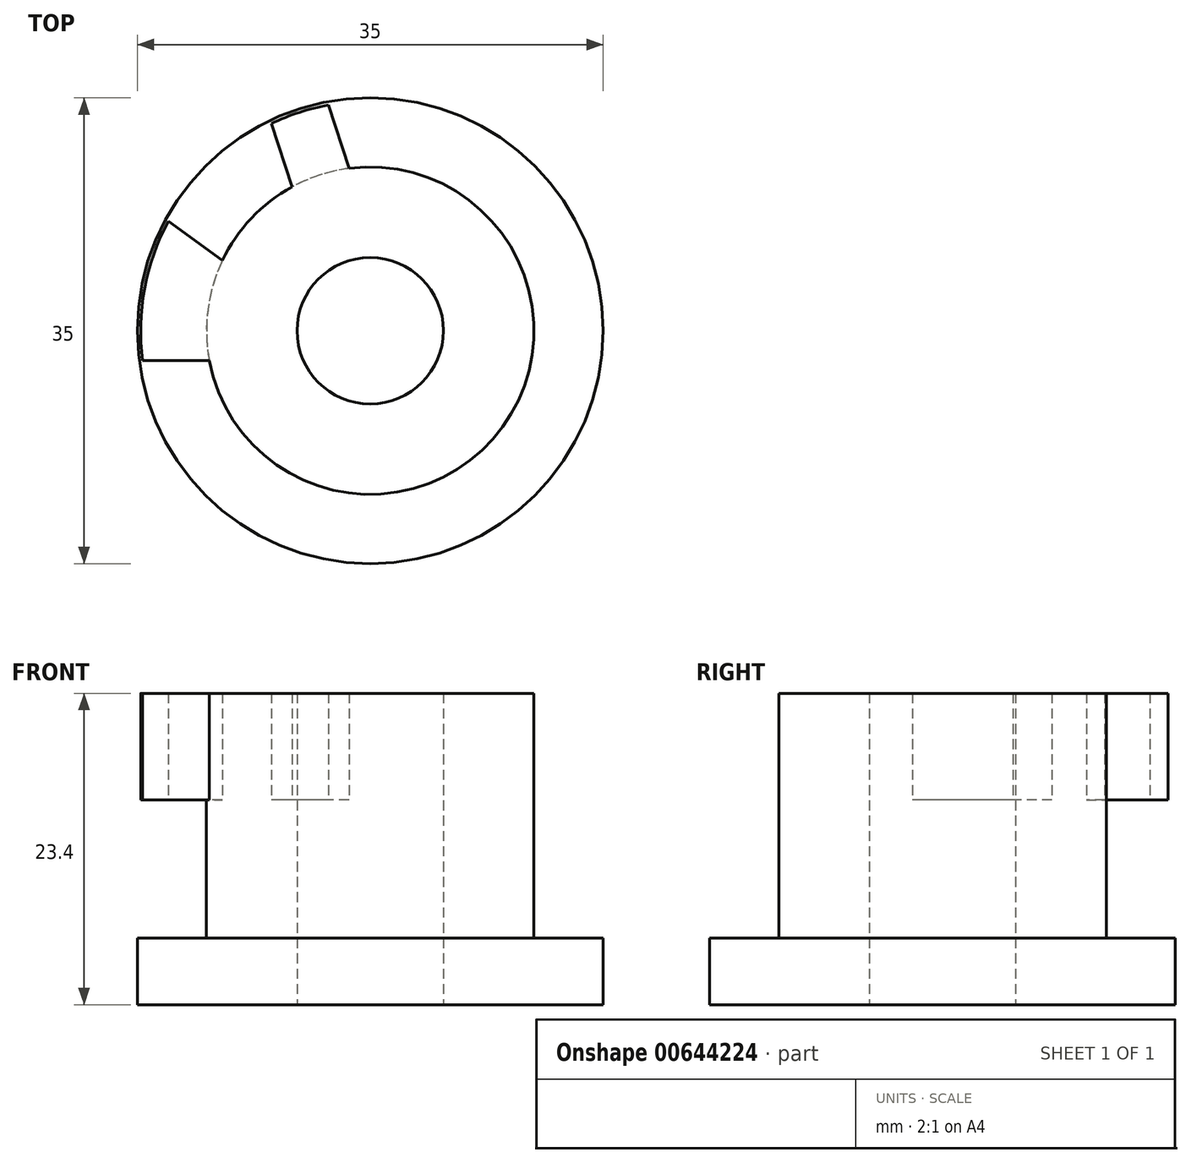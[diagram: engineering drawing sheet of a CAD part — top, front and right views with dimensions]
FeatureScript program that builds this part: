
annotation { "Feature Type Name" : "Feature", "Feature Type Description" : "" }
export const myFeature = defineFeature(function(context is Context, id is Id, definition is map)
    precondition{}
    {
        {
            var Q0;
            Q0=qCreatedBy(makeId("Top.planeOp"),FACE);
            var sketch = newSketch(context, id + "F0", { "sketchPlane" : qUnion([Q0])});
            skCircle(sketch, "E0", {"center": v(0, 0) * mm, "radius": 17.5 * mm});
            skCircle(sketch, "E1", {"center": v(0, 0) * mm, "radius": 5.5 * mm});
            skSolve(sketch);
        }
        {
            var Q0;
            Q0=makeQuery(id+"F0.imprint","IMPRINT",FACE,{"disambiguationData":[TD([[makeQuery(id+"F0.imprint","IMPRINT",EDGE,{"derivedFrom":sQuery(id+"F0.wireOp",EDGE,"E0")}),1.0]])]});
            extrude(context, id + "F1", {"entities" : qUnion([Q0]), "depth" : 5 * mm, "offsetDistance" : 25 * mm});
        }
        {
            var Q0;
            Q0=makeQuery(id+"F1.opExtrude","CAP_FACE",FACE,{"disambiguationData":[OSD([sQuery(id+"F0.wireOp",EDGE,"E0")])],"isStart":false});
            var sketch = newSketch(context, id + "F2", { "sketchPlane" : qUnion([Q0])});
            skCircle(sketch, "E2", {"center": v(0, 0) * mm, "radius": 12.3 * mm});
            skSolve(sketch);
        }
        {
            var Q0;
            Q0=makeQuery(id+"F2.imprint","IMPRINT",FACE,{"disambiguationData":[TD([[makeQuery(id+"F2.imprint","IMPRINT",EDGE,{"derivedFrom":sQuery(id+"F2.wireOp",EDGE,"E2")}),1.0]])]});
            var Q1;
            Q1=sQuery(id+"F2.wireOp",EDGE,"E2");
            extrude(context, id + "F3", {"entities" : qUnion([Q0]), "surfaceEntities" : qUnion([Q1]), "depth" : 10.4 * mm, "offsetDistance" : 25 * mm});
        }
        {
            var Q0;
            Q0=makeQuery(id+"F3.opExtrude","CAP_FACE",FACE,{"disambiguationData":[OSD([sQuery(id+"F2.wireOp",EDGE,"E2")])],"isStart":false});
            var sketch = newSketch(context, id + "F4", { "sketchPlane" : qUnion([Q0])});
            skPoint(sketch, "E3.middle", {"position": v(0, 0) * mm});
            skLineSegment(sketch, "E4.bottom", {"start": v(24.05, -2.25) * mm, "end": v(-24.05, -2.25) * mm});
            skLineSegment(sketch, "E4.top", {"start": v(24.05, 2.25) * mm, "end": v(-24.05, 2.25) * mm});
            skLineSegment(sketch, "E4.left", {"start": v(24.05, -2.25) * mm, "end": v(24.05, 2.25) * mm});
            skLineSegment(sketch, "E4.right", {"start": v(-24.05, -2.25) * mm, "end": v(-24.05, 2.25) * mm});
            skCircle(sketch, "E5", {"center": v(0, 0) * mm, "radius": 17.25 * mm});
            skLineSegment(sketch, "E6.1.0", {"start": v(5.3, 23.57) * mm, "end": v(-9.57, -22.18) * mm});
            skLineSegment(sketch, "E6.1.1", {"start": v(-5.3, -23.57) * mm, "end": v(-9.57, -22.18) * mm});
            skLineSegment(sketch, "E6.1.2", {"start": v(9.57, 22.18) * mm, "end": v(-5.3, -23.57) * mm});
            skLineSegment(sketch, "E6.1.3", {"start": v(9.57, 22.18) * mm, "end": v(5.3, 23.57) * mm});
            skLineSegment(sketch, "E6.2.0", {"start": v(-20.78, 12.32) * mm, "end": v(18.14, -15.96) * mm});
            skLineSegment(sketch, "E6.2.1", {"start": v(20.78, -12.32) * mm, "end": v(18.14, -15.96) * mm});
            skLineSegment(sketch, "E6.2.2", {"start": v(-18.14, 15.96) * mm, "end": v(20.78, -12.32) * mm});
            skLineSegment(sketch, "E6.2.3", {"start": v(-18.14, 15.96) * mm, "end": v(-20.78, 12.32) * mm});
            skLineSegment(sketch, "E6.3.0", {"start": v(-18.14, -15.96) * mm, "end": v(20.78, 12.32) * mm});
            skLineSegment(sketch, "E6.3.1", {"start": v(18.14, 15.96) * mm, "end": v(20.78, 12.32) * mm});
            skLineSegment(sketch, "E6.3.2", {"start": v(-20.78, -12.32) * mm, "end": v(18.14, 15.96) * mm});
            skLineSegment(sketch, "E6.3.3", {"start": v(-20.78, -12.32) * mm, "end": v(-18.14, -15.96) * mm});
            skLineSegment(sketch, "E6.4.0", {"start": v(9.57, -22.18) * mm, "end": v(-5.3, 23.57) * mm});
            skLineSegment(sketch, "E6.4.1", {"start": v(-9.57, 22.18) * mm, "end": v(-5.3, 23.57) * mm});
            skLineSegment(sketch, "E6.4.2", {"start": v(5.3, -23.57) * mm, "end": v(-9.57, 22.18) * mm});
            skLineSegment(sketch, "E6.4.3", {"start": v(5.3, -23.57) * mm, "end": v(9.57, -22.18) * mm});
            skSolve(sketch);
        }
        {
            var Q0;
            {var subQ0=sQuery(id+"F4.wireOp",EDGE,"E6.4.0");var subQ1=sQuery(id+"F4.wireOp",EDGE,"E5");var subQ2=makeQuery(id+"F4.imprint","INTERSECT",VERTEX,{"disambiguationData":[OD(0.0)],"derivedFrom":[subQ1,subQ0]});Q0=makeQuery(id+"F4.imprint","IMPRINT",FACE,{"disambiguationData":[TD([[makeQuery(id+"F4.imprint","IMPRINT",EDGE,{"disambiguationData":[TD([[subQ2,-1.0]])],"derivedFrom":subQ1}),1.0]])]});}
            var Q1;
            {var subQ0=sQuery(id+"F4.wireOp",EDGE,"E5");var subQ1=sQuery(id+"F4.wireOp",EDGE,"E4.bottom");var subQ2=makeQuery(id+"F4.imprint","INTERSECT",VERTEX,{"disambiguationData":[OD(1.0)],"derivedFrom":[subQ1,subQ0]});Q1=makeQuery(id+"F4.imprint","IMPRINT",FACE,{"disambiguationData":[TD([[makeQuery(id+"F4.imprint","IMPRINT",EDGE,{"disambiguationData":[TD([[subQ2,1.0]])],"derivedFrom":subQ1}),-1.0]])]});}
            var Q2;
            {var subQ0=sQuery(id+"F4.wireOp",EDGE,"E6.2.0");var subQ1=sQuery(id+"F4.wireOp",EDGE,"E5");var subQ2=makeQuery(id+"F4.imprint","INTERSECT",VERTEX,{"disambiguationData":[OD(1.0)],"derivedFrom":[subQ1,subQ0]});Q2=makeQuery(id+"F4.imprint","IMPRINT",FACE,{"disambiguationData":[TD([[makeQuery(id+"F4.imprint","IMPRINT",EDGE,{"disambiguationData":[TD([[subQ2,-1.0]])],"derivedFrom":subQ1}),1.0]])]});}
            var Q3;
            {var subQ0=sQuery(id+"F4.wireOp",EDGE,"E6.2.2");var subQ1=sQuery(id+"F4.wireOp",EDGE,"E4.bottom");var subQ2=makeQuery(id+"F4.imprint","INTERSECT",VERTEX,{"derivedFrom":[subQ1,subQ0]});Q3=makeQuery(id+"F4.imprint","IMPRINT",FACE,{"disambiguationData":[TD([[makeQuery(id+"F4.imprint","IMPRINT",EDGE,{"disambiguationData":[TD([[subQ2,-1.0]])],"derivedFrom":subQ1}),1.0]])]});}
            var Q4;
            {var subQ0=sQuery(id+"F4.wireOp",EDGE,"E6.2.2");var subQ1=sQuery(id+"F4.wireOp",EDGE,"E4.bottom");var subQ2=makeQuery(id+"F4.imprint","INTERSECT",VERTEX,{"derivedFrom":[subQ1,subQ0]});Q4=makeQuery(id+"F4.imprint","IMPRINT",FACE,{"disambiguationData":[TD([[makeQuery(id+"F4.imprint","IMPRINT",EDGE,{"disambiguationData":[TD([[subQ2,1.0]])],"derivedFrom":subQ1}),1.0]])]});}
            var Q5;
            {var subQ0=sQuery(id+"F4.wireOp",EDGE,"E6.2.2");var subQ1=sQuery(id+"F4.wireOp",EDGE,"E4.bottom");var subQ2=makeQuery(id+"F4.imprint","INTERSECT",VERTEX,{"derivedFrom":[subQ1,subQ0]});Q5=makeQuery(id+"F4.imprint","IMPRINT",FACE,{"disambiguationData":[TD([[makeQuery(id+"F4.imprint","IMPRINT",EDGE,{"disambiguationData":[TD([[subQ2,1.0]])],"derivedFrom":subQ1}),-1.0]])]});}
            var Q6;
            {var subQ0=sQuery(id+"F4.wireOp",EDGE,"E6.3.0");var subQ1=sQuery(id+"F4.wireOp",EDGE,"E4.top");var subQ2=makeQuery(id+"F4.imprint","INTERSECT",VERTEX,{"derivedFrom":[subQ1,subQ0]});Q6=makeQuery(id+"F4.imprint","IMPRINT",FACE,{"disambiguationData":[TD([[makeQuery(id+"F4.imprint","IMPRINT",EDGE,{"disambiguationData":[TD([[subQ2,1.0]])],"derivedFrom":subQ1}),-1.0]])]});}
            var Q7;
            {var subQ7=sQuery(id+"F4.wireOp",EDGE,"E6.3.0");var subQ8=sQuery(id+"F4.wireOp",EDGE,"E4.top");var subQ9=makeQuery(id+"F4.imprint","INTERSECT",VERTEX,{"derivedFrom":[subQ8,subQ7]});Q7=makeQuery(id+"F4.imprint","IMPRINT",FACE,{"disambiguationData":[TD([[makeQuery(id+"F4.imprint","IMPRINT",EDGE,{"disambiguationData":[TD([[subQ9,-1.0]])],"derivedFrom":subQ8}),-1.0]])]});}
            var Q8;
            {var subQ0=sQuery(id+"F4.wireOp",EDGE,"E6.3.2");var subQ1=sQuery(id+"F4.wireOp",EDGE,"E6.1.2");var subQ2=makeQuery(id+"F4.imprint","INTERSECT",VERTEX,{"derivedFrom":[subQ1,subQ0]});Q8=makeQuery(id+"F4.imprint","IMPRINT",FACE,{"disambiguationData":[TD([[makeQuery(id+"F4.imprint","IMPRINT",EDGE,{"disambiguationData":[TD([[subQ2,1.0]])],"derivedFrom":subQ1}),1.0]])]});}
            var Q9;
            {var subQ7=sQuery(id+"F4.wireOp",EDGE,"E6.4.0");var subQ8=sQuery(id+"F4.wireOp",EDGE,"E6.1.0");var subQ9=makeQuery(id+"F4.imprint","INTERSECT",VERTEX,{"derivedFrom":[subQ8,subQ7]});Q9=makeQuery(id+"F4.imprint","IMPRINT",FACE,{"disambiguationData":[TD([[makeQuery(id+"F4.imprint","IMPRINT",EDGE,{"disambiguationData":[TD([[subQ9,1.0]])],"derivedFrom":subQ8}),1.0]])]});}
            var Q10;
            {var subQ0=sQuery(id+"F4.wireOp",EDGE,"E6.4.0");var subQ1=sQuery(id+"F4.wireOp",EDGE,"E6.1.0");var subQ2=makeQuery(id+"F4.imprint","INTERSECT",VERTEX,{"derivedFrom":[subQ1,subQ0]});Q10=makeQuery(id+"F4.imprint","IMPRINT",FACE,{"disambiguationData":[TD([[makeQuery(id+"F4.imprint","IMPRINT",EDGE,{"disambiguationData":[TD([[subQ2,1.0]])],"derivedFrom":subQ1}),-1.0]])]});}
            var Q11;
            {var subQ5=sQuery(id+"F4.wireOp",EDGE,"E6.4.0");var subQ6=sQuery(id+"F4.wireOp",EDGE,"E6.1.0");var subQ7=makeQuery(id+"F4.imprint","INTERSECT",VERTEX,{"derivedFrom":[subQ6,subQ5]});Q11=makeQuery(id+"F4.imprint","IMPRINT",FACE,{"disambiguationData":[TD([[makeQuery(id+"F4.imprint","IMPRINT",EDGE,{"disambiguationData":[TD([[subQ7,-1.0]])],"derivedFrom":subQ6}),-1.0]])]});}
            var Q12;
            {var subQ0=sQuery(id+"F4.wireOp",EDGE,"E6.4.2");var subQ1=sQuery(id+"F4.wireOp",EDGE,"E6.2.2");var subQ2=makeQuery(id+"F4.imprint","INTERSECT",VERTEX,{"derivedFrom":[subQ1,subQ0]});Q12=makeQuery(id+"F4.imprint","IMPRINT",FACE,{"disambiguationData":[TD([[makeQuery(id+"F4.imprint","IMPRINT",EDGE,{"disambiguationData":[TD([[subQ2,1.0]])],"derivedFrom":subQ1}),1.0]])]});}
            var Q13;
            {var subQ7=sQuery(id+"F4.wireOp",EDGE,"E6.2.0");var subQ8=sQuery(id+"F4.wireOp",EDGE,"E4.top");var subQ9=makeQuery(id+"F4.imprint","INTERSECT",VERTEX,{"derivedFrom":[subQ8,subQ7]});Q13=makeQuery(id+"F4.imprint","IMPRINT",FACE,{"disambiguationData":[TD([[makeQuery(id+"F4.imprint","IMPRINT",EDGE,{"disambiguationData":[TD([[subQ9,1.0]])],"derivedFrom":subQ8}),-1.0]])]});}
            var Q14;
            {var subQ0=sQuery(id+"F4.wireOp",EDGE,"E6.2.0");var subQ1=sQuery(id+"F4.wireOp",EDGE,"E4.top");var subQ2=makeQuery(id+"F4.imprint","INTERSECT",VERTEX,{"derivedFrom":[subQ1,subQ0]});Q14=makeQuery(id+"F4.imprint","IMPRINT",FACE,{"disambiguationData":[TD([[makeQuery(id+"F4.imprint","IMPRINT",EDGE,{"disambiguationData":[TD([[subQ2,-1.0]])],"derivedFrom":subQ1}),-1.0]])]});}
            var Q15;
            {var subQ0=sQuery(id+"F4.wireOp",EDGE,"E6.3.2");var subQ1=sQuery(id+"F4.wireOp",EDGE,"E4.bottom");var subQ2=makeQuery(id+"F4.imprint","INTERSECT",VERTEX,{"derivedFrom":[subQ1,subQ0]});Q15=makeQuery(id+"F4.imprint","IMPRINT",FACE,{"disambiguationData":[TD([[makeQuery(id+"F4.imprint","IMPRINT",EDGE,{"disambiguationData":[TD([[subQ2,-1.0]])],"derivedFrom":subQ1}),-1.0]])]});}
            var Q16;
            {var subQ0=sQuery(id+"F4.wireOp",EDGE,"E6.3.2");var subQ1=sQuery(id+"F4.wireOp",EDGE,"E4.bottom");var subQ2=makeQuery(id+"F4.imprint","INTERSECT",VERTEX,{"derivedFrom":[subQ1,subQ0]});Q16=makeQuery(id+"F4.imprint","IMPRINT",FACE,{"disambiguationData":[TD([[makeQuery(id+"F4.imprint","IMPRINT",EDGE,{"disambiguationData":[TD([[subQ2,-1.0]])],"derivedFrom":subQ1}),1.0]])]});}
            var Q17;
            {var subQ0=sQuery(id+"F4.wireOp",EDGE,"E6.3.2");var subQ1=sQuery(id+"F4.wireOp",EDGE,"E4.bottom");var subQ2=makeQuery(id+"F4.imprint","INTERSECT",VERTEX,{"derivedFrom":[subQ1,subQ0]});Q17=makeQuery(id+"F4.imprint","IMPRINT",FACE,{"disambiguationData":[TD([[makeQuery(id+"F4.imprint","IMPRINT",EDGE,{"disambiguationData":[TD([[subQ2,1.0]])],"derivedFrom":subQ1}),1.0]])]});}
            var Q18;
            {var subQ0=sQuery(id+"F4.wireOp",EDGE,"E6.3.0");var subQ1=sQuery(id+"F4.wireOp",EDGE,"E6.1.0");var subQ2=makeQuery(id+"F4.imprint","INTERSECT",VERTEX,{"derivedFrom":[subQ1,subQ0]});Q18=makeQuery(id+"F4.imprint","IMPRINT",FACE,{"disambiguationData":[TD([[makeQuery(id+"F4.imprint","IMPRINT",EDGE,{"disambiguationData":[TD([[subQ2,-1.0]])],"derivedFrom":subQ1}),-1.0]])]});}
            var Q19;
            {var subQ7=sQuery(id+"F4.wireOp",EDGE,"E6.3.0");var subQ8=sQuery(id+"F4.wireOp",EDGE,"E6.1.0");var subQ9=makeQuery(id+"F4.imprint","INTERSECT",VERTEX,{"derivedFrom":[subQ8,subQ7]});Q19=makeQuery(id+"F4.imprint","IMPRINT",FACE,{"disambiguationData":[TD([[makeQuery(id+"F4.imprint","IMPRINT",EDGE,{"disambiguationData":[TD([[subQ9,-1.0]])],"derivedFrom":subQ8}),1.0]])]});}
            var Q20;
            {var subQ0=sQuery(id+"F4.wireOp",EDGE,"E6.4.2");var subQ1=sQuery(id+"F4.wireOp",EDGE,"E6.1.2");var subQ2=makeQuery(id+"F4.imprint","INTERSECT",VERTEX,{"derivedFrom":[subQ1,subQ0]});Q20=makeQuery(id+"F4.imprint","IMPRINT",FACE,{"disambiguationData":[TD([[makeQuery(id+"F4.imprint","IMPRINT",EDGE,{"disambiguationData":[TD([[subQ2,-1.0]])],"derivedFrom":subQ1}),1.0]])]});}
            var Q21;
            {var subQ0=sQuery(id+"F4.wireOp",EDGE,"E6.4.2");var subQ1=sQuery(id+"F4.wireOp",EDGE,"E6.1.2");var subQ2=makeQuery(id+"F4.imprint","INTERSECT",VERTEX,{"derivedFrom":[subQ1,subQ0]});Q21=makeQuery(id+"F4.imprint","IMPRINT",FACE,{"disambiguationData":[TD([[makeQuery(id+"F4.imprint","IMPRINT",EDGE,{"disambiguationData":[TD([[subQ2,1.0]])],"derivedFrom":subQ1}),1.0]])]});}
            var Q22;
            {var subQ0=sQuery(id+"F4.wireOp",EDGE,"E6.4.0");var subQ1=sQuery(id+"F4.wireOp",EDGE,"E6.2.0");var subQ2=makeQuery(id+"F4.imprint","INTERSECT",VERTEX,{"derivedFrom":[subQ1,subQ0]});Q22=makeQuery(id+"F4.imprint","IMPRINT",FACE,{"disambiguationData":[TD([[makeQuery(id+"F4.imprint","IMPRINT",EDGE,{"disambiguationData":[TD([[subQ2,-1.0]])],"derivedFrom":subQ1}),-1.0]])]});}
            var Q23;
            {var subQ0=sQuery(id+"F4.wireOp",EDGE,"E6.4.0");var subQ1=sQuery(id+"F4.wireOp",EDGE,"E6.2.0");var subQ2=makeQuery(id+"F4.imprint","INTERSECT",VERTEX,{"derivedFrom":[subQ1,subQ0]});Q23=makeQuery(id+"F4.imprint","IMPRINT",FACE,{"disambiguationData":[TD([[makeQuery(id+"F4.imprint","IMPRINT",EDGE,{"disambiguationData":[TD([[subQ2,1.0]])],"derivedFrom":subQ1}),1.0]])]});}
            var Q24;
            {var subQ0=sQuery(id+"F4.wireOp",EDGE,"E6.2.2");var subQ1=sQuery(id+"F4.wireOp",EDGE,"E4.bottom");var subQ2=makeQuery(id+"F4.imprint","INTERSECT",VERTEX,{"derivedFrom":[subQ1,subQ0]});Q24=makeQuery(id+"F4.imprint","IMPRINT",FACE,{"disambiguationData":[TD([[makeQuery(id+"F4.imprint","IMPRINT",EDGE,{"disambiguationData":[TD([[subQ2,-1.0]])],"derivedFrom":subQ1}),-1.0]])]});}
            var Q25;
            {var subQ0=sQuery(id+"F4.wireOp",EDGE,"E6.3.0");var subQ1=sQuery(id+"F4.wireOp",EDGE,"E4.top");var subQ2=makeQuery(id+"F4.imprint","INTERSECT",VERTEX,{"derivedFrom":[subQ1,subQ0]});Q25=makeQuery(id+"F4.imprint","IMPRINT",FACE,{"disambiguationData":[TD([[makeQuery(id+"F4.imprint","IMPRINT",EDGE,{"disambiguationData":[TD([[subQ2,-1.0]])],"derivedFrom":subQ1}),1.0]])]});}
            var Q26;
            {var subQ0=sQuery(id+"F4.wireOp",EDGE,"E6.3.2");var subQ1=sQuery(id+"F4.wireOp",EDGE,"E6.1.2");var subQ2=makeQuery(id+"F4.imprint","INTERSECT",VERTEX,{"derivedFrom":[subQ1,subQ0]});Q26=makeQuery(id+"F4.imprint","IMPRINT",FACE,{"disambiguationData":[TD([[makeQuery(id+"F4.imprint","IMPRINT",EDGE,{"disambiguationData":[TD([[subQ2,-1.0]])],"derivedFrom":subQ1}),-1.0]])]});}
            var Q27;
            {var subQ0=sQuery(id+"F4.wireOp",EDGE,"E6.4.0");var subQ1=sQuery(id+"F4.wireOp",EDGE,"E6.1.0");var subQ2=makeQuery(id+"F4.imprint","INTERSECT",VERTEX,{"derivedFrom":[subQ1,subQ0]});Q27=makeQuery(id+"F4.imprint","IMPRINT",FACE,{"disambiguationData":[TD([[makeQuery(id+"F4.imprint","IMPRINT",EDGE,{"disambiguationData":[TD([[subQ2,-1.0]])],"derivedFrom":subQ1}),1.0]])]});}
            var Q28;
            {var subQ0=sQuery(id+"F4.wireOp",EDGE,"E6.4.2");var subQ1=sQuery(id+"F4.wireOp",EDGE,"E6.2.2");var subQ2=makeQuery(id+"F4.imprint","INTERSECT",VERTEX,{"derivedFrom":[subQ1,subQ0]});Q28=makeQuery(id+"F4.imprint","IMPRINT",FACE,{"disambiguationData":[TD([[makeQuery(id+"F4.imprint","IMPRINT",EDGE,{"disambiguationData":[TD([[subQ2,-1.0]])],"derivedFrom":subQ1}),-1.0]])]});}
            var Q29;
            {var subQ0=sQuery(id+"F4.wireOp",EDGE,"E6.2.0");var subQ1=sQuery(id+"F4.wireOp",EDGE,"E4.top");var subQ2=makeQuery(id+"F4.imprint","INTERSECT",VERTEX,{"derivedFrom":[subQ1,subQ0]});Q29=makeQuery(id+"F4.imprint","IMPRINT",FACE,{"disambiguationData":[TD([[makeQuery(id+"F4.imprint","IMPRINT",EDGE,{"disambiguationData":[TD([[subQ2,1.0]])],"derivedFrom":subQ1}),1.0]])]});}
            var Q30;
            {var subQ0=sQuery(id+"F4.wireOp",EDGE,"E6.3.2");var subQ1=sQuery(id+"F4.wireOp",EDGE,"E4.bottom");var subQ2=makeQuery(id+"F4.imprint","INTERSECT",VERTEX,{"derivedFrom":[subQ1,subQ0]});Q30=makeQuery(id+"F4.imprint","IMPRINT",FACE,{"disambiguationData":[TD([[makeQuery(id+"F4.imprint","IMPRINT",EDGE,{"disambiguationData":[TD([[subQ2,1.0]])],"derivedFrom":subQ1}),-1.0]])]});}
            var Q31;
            {var subQ0=sQuery(id+"F4.wireOp",EDGE,"E6.3.0");var subQ1=sQuery(id+"F4.wireOp",EDGE,"E6.1.0");var subQ2=makeQuery(id+"F4.imprint","INTERSECT",VERTEX,{"derivedFrom":[subQ1,subQ0]});Q31=makeQuery(id+"F4.imprint","IMPRINT",FACE,{"disambiguationData":[TD([[makeQuery(id+"F4.imprint","IMPRINT",EDGE,{"disambiguationData":[TD([[subQ2,1.0]])],"derivedFrom":subQ1}),1.0]])]});}
            var Q32;
            {var subQ0=sQuery(id+"F4.wireOp",EDGE,"E6.4.2");var subQ1=sQuery(id+"F4.wireOp",EDGE,"E6.1.2");var subQ2=makeQuery(id+"F4.imprint","INTERSECT",VERTEX,{"derivedFrom":[subQ1,subQ0]});Q32=makeQuery(id+"F4.imprint","IMPRINT",FACE,{"disambiguationData":[TD([[makeQuery(id+"F4.imprint","IMPRINT",EDGE,{"disambiguationData":[TD([[subQ2,1.0]])],"derivedFrom":subQ1}),-1.0]])]});}
            extrude(context, id + "F5", {"entities" : qUnion([Q0, Q1, Q2, Q3, Q4, Q5, Q6, Q7, Q8, Q9, Q10, Q11, Q12, Q13, Q14, Q15, Q16, Q17, Q18, Q19, Q20, Q21, Q22, Q23, Q24, Q25, Q26, Q27, Q28, Q29, Q30, Q31, Q32]), "operationType" : NewBodyOperationType.ADD, "depth" : 8 * mm, "offsetDistance" : 25 * mm});
        }
    });
